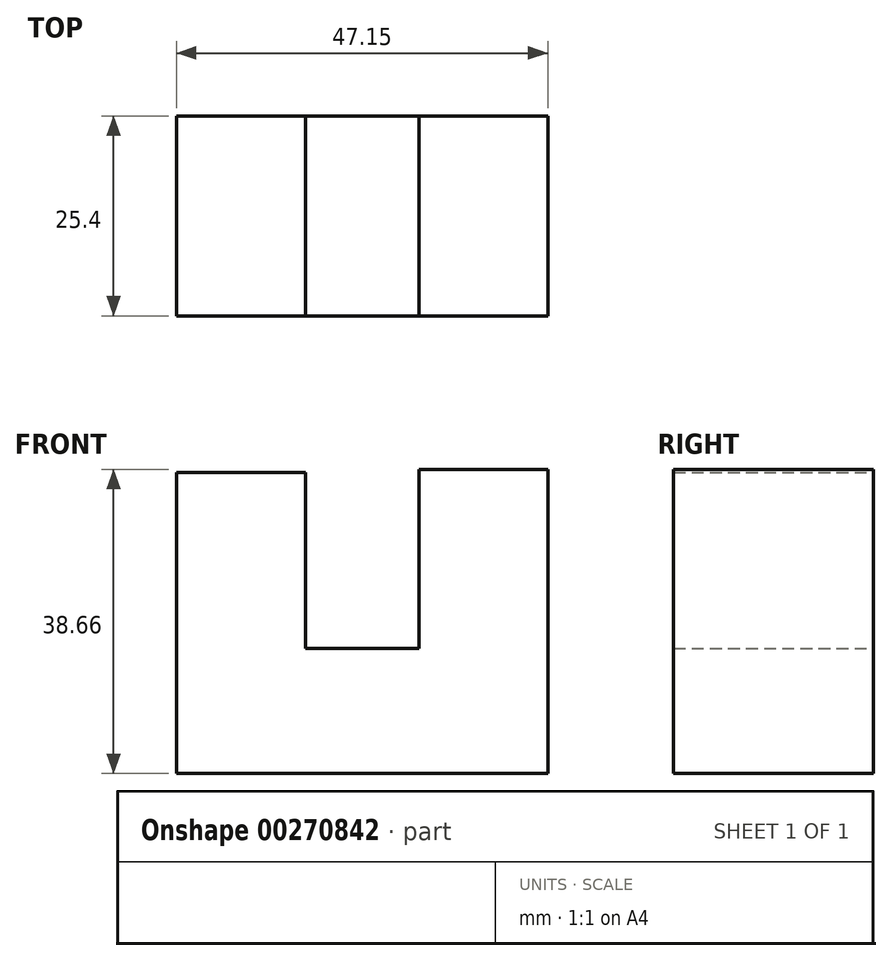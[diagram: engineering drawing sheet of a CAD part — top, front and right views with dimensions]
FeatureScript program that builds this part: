
annotation { "Feature Type Name" : "Feature", "Feature Type Description" : "" }
export const myFeature = defineFeature(function(context is Context, id is Id, definition is map)
    precondition{}
    {
        {
            var Q0;
            Q0=qCreatedBy(makeId("Front.planeOp"),FACE);
            var sketch = newSketch(context, id + "F0", { "sketchPlane" : qUnion([Q0])});
            skLineSegment(sketch, "E0", {"start": v(0, 0) * mm, "end": v(0, 38.66) * mm});
            skLineSegment(sketch, "E1", {"start": v(0, 38.66) * mm, "end": v(-16.38, 38.66) * mm});
            skLineSegment(sketch, "E2", {"start": v(-16.38, 38.66) * mm, "end": v(-16.38, 15.88) * mm});
            skLineSegment(sketch, "E3", {"start": v(-16.38, 15.88) * mm, "end": v(-30.77, 15.88) * mm});
            skLineSegment(sketch, "E4", {"start": v(-30.77, 15.88) * mm, "end": v(-30.77, 38.26) * mm});
            skLineSegment(sketch, "E5", {"start": v(-30.77, 38.26) * mm, "end": v(-47.15, 38.26) * mm});
            skLineSegment(sketch, "E6", {"start": v(-47.15, 38.26) * mm, "end": v(-47.15, 0) * mm});
            skLineSegment(sketch, "E7", {"start": v(-47.15, 0) * mm, "end": v(1.4, 0) * mm});
            skSolve(sketch);
        }
        {
            var Q0;
            {var subQ0=sQuery(id+"F0.wireOp",EDGE,"E0");Q0=makeQuery(id+"F0.imprint","IMPRINT",FACE,{"disambiguationData":[TD([[makeQuery(id+"F0.imprint","IMPRINT",EDGE,{"derivedFrom":subQ0}),1.0]])]});}
            extrude(context, id + "F1", {"entities" : qUnion([Q0]), "depth" : 25.4 * mm});
        }
    });
